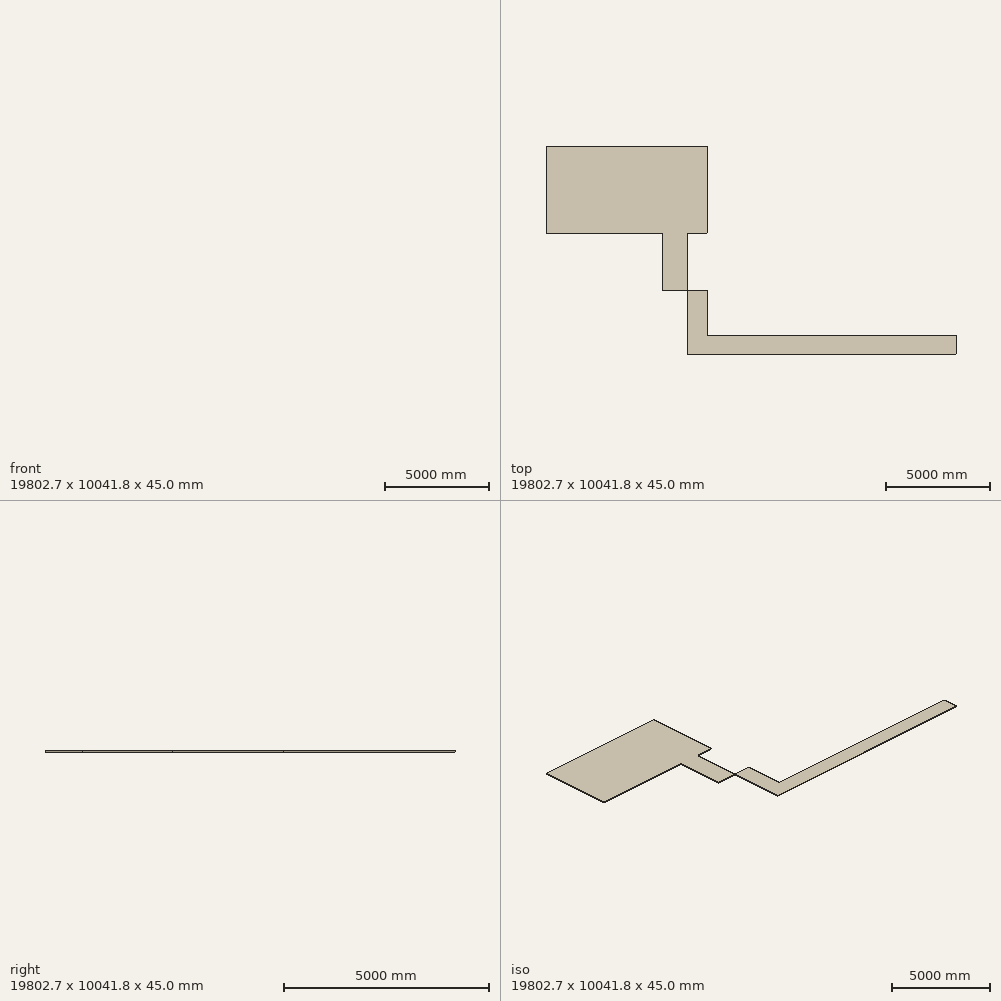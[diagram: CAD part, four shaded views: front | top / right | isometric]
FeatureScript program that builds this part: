
annotation { "Feature Type Name" : "Feature", "Feature Type Description" : "" }
export const myFeature = defineFeature(function(context is Context, id is Id, definition is map)
    precondition{}
    {
        {
            var Q0;
            Q0=qCreatedBy(makeId("Top.planeOp"),FACE);
            var sketch = newSketch(context, id + "F0", { "sketchPlane" : qUnion([Q0])});
            skLineSegment(sketch, "E0", {"start": v(0, 3902.83) * mm, "end": v(-7800, 3902.83) * mm});
            skLineSegment(sketch, "E1", {"start": v(-7800, 3902.83) * mm, "end": v(-7800, -297.17) * mm});
            skLineSegment(sketch, "E2", {"start": v(0, 3902.83) * mm, "end": v(0, -297.17) * mm});
            skLineSegment(sketch, "E3", {"start": v(0, -297.17) * mm, "end": v(-1000, -297.17) * mm});
            skLineSegment(sketch, "E4", {"start": v(-1000, -297.17) * mm, "end": v(-1000, -3038.97) * mm});
            skLineSegment(sketch, "E5", {"start": v(-1000, -3038.97) * mm, "end": v(0, -3038.97) * mm});
            skLineSegment(sketch, "E6", {"start": v(0, -3038.97) * mm, "end": v(0, -5238.97) * mm});
            skLineSegment(sketch, "E7", {"start": v(-7800, -297.17) * mm, "end": v(-2200, -297.17) * mm});
            skLineSegment(sketch, "E8", {"start": v(-2200, -297.17) * mm, "end": v(-2200, -3040.02) * mm});
            skLineSegment(sketch, "E9", {"start": v(-2200, -3040.02) * mm, "end": v(-1000, -3038.97) * mm});
            skLineSegment(sketch, "E10", {"start": v(-1000, -3038.97) * mm, "end": v(-997.27, -6138.96) * mm});
            skLineSegment(sketch, "E11", {"start": v(-997.27, -6138.96) * mm, "end": v(12002.72, -6127.52) * mm});
            skLineSegment(sketch, "E12", {"start": v(0, -5238.97) * mm, "end": v(12002.72, -5238.97) * mm});
            skLineSegment(sketch, "E13", {"start": v(12002.72, -5238.97) * mm, "end": v(12002.72, -6127.52) * mm});
            skSolve(sketch);
        }
        {
            var Q0;
            Q0=makeQuery(id+"F0.imprint","IMPRINT",FACE,{"disambiguationData":[TD([[makeQuery(id+"F0.imprint","IMPRINT",EDGE,{"derivedFrom":sQuery(id+"F0.wireOp",EDGE,"E5")}),-1.0]])]});
            var Q1;
            Q1=makeQuery(id+"F0.imprint","IMPRINT",FACE,{"disambiguationData":[TD([[makeQuery(id+"F0.imprint","IMPRINT",EDGE,{"derivedFrom":sQuery(id+"F0.wireOp",EDGE,"E0")}),1.0]])]});
            extrude(context, id + "F1", {"entities" : qUnion([Q0, Q1]), "depth" : 45 * mm, "offsetDistance" : 25 * mm});
        }
    });
